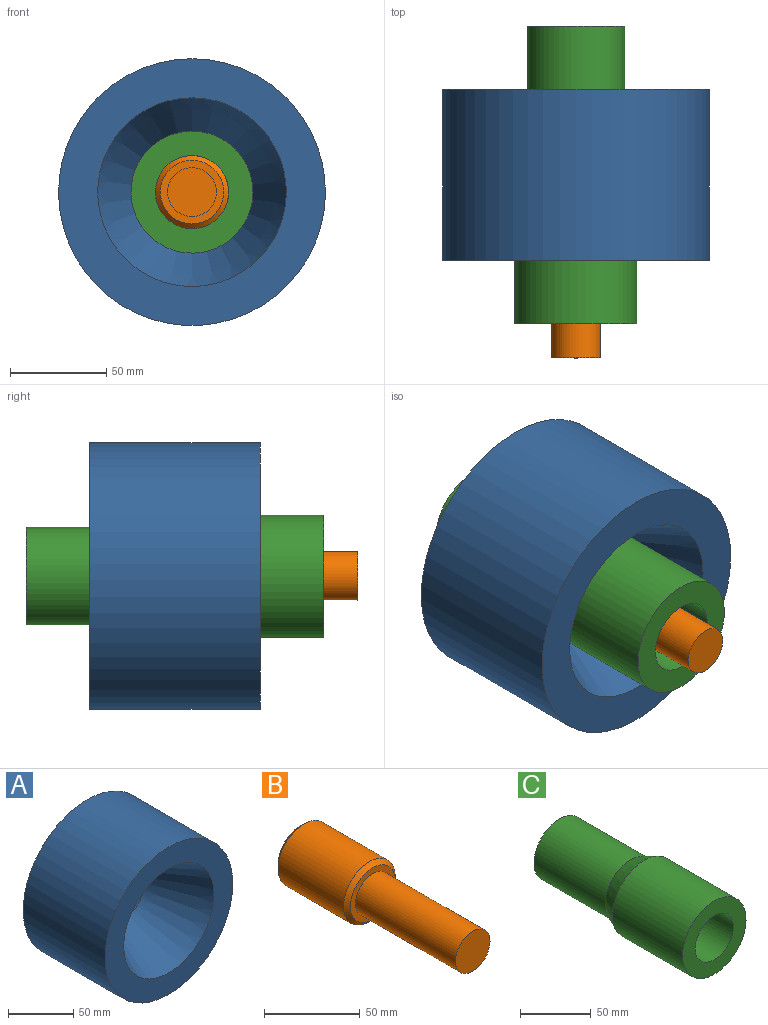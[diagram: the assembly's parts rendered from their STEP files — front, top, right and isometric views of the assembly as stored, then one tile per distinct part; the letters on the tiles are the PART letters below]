
ASSEMBLY  parts=3 mates=4
PART A: 6 faces, bbox 138.8x88.9x138.8 mm
  f0: cylinder r=69.42mm len=138.84mm, axis (0,1,0), area 38777.5mm2, adj f1,f5
  f1: plane 138.84x138.84mm, normal (0,-1,0), area 7570.5mm2, adj f0,f2
  f2: cone r=25.4mm half-angle=25deg, axis (0,-1,0), area 13116.8mm2, adj f1,f3
  f3: cylinder r=25.4mm len=50.8mm, axis (0,1,0), area 4053.7mm2, adj f2,f4
  f4: cone r=25.4mm half-angle=25deg, axis (0,1,0), area 2497.1mm2, adj f3,f5
  f5: plane 138.84x138.84mm, normal (0,1,0), area 12058.5mm2, adj f0,f4
PART B: 7 faces, bbox 38.1x127x38.1 mm
  f0: plane 33.02x33.02mm, normal (0,1,0), area 856.3mm2, adj f6
  f1: cylinder r=19.05mm len=48.26mm, axis (0,1,0), area 5776.5mm2, adj f5,f6
  f2: plane 33.02x33.02mm, normal (0,-1,0), area 349.6mm2, adj f3,f5
  f3: cylinder r=12.7mm len=73.66mm, axis (0,1,0), area 5877.8mm2, adj f2,f4
  f4: plane 25.4x25.4mm, normal (0,-1,0), area 506.7mm2, adj f3
  f5: cone r=19.05mm half-angle=45deg, axis (0,1,0), area 401.3mm2, adj f1,f2
  f6: cone r=16.51mm half-angle=45deg, axis (0,-1,0), area 401.3mm2, adj f0,f1
PART C: 6 faces, bbox 63.5x154.9x63.5 mm
  f0: plane 50.8x50.8mm, normal (0,1,0), area 886.7mm2, adj f1,f5
  f1: cylinder r=25.4mm len=71.12mm, axis (0,1,0), area 11350.2mm2, adj f0,f2
  f2: cone r=25.4mm half-angle=25deg, axis (0,-1,0), area 2697.7mm2, adj f1,f3
  f3: cylinder r=31.75mm len=70.2mm, axis (0,1,0), area 14004.8mm2, adj f2,f4
  f4: plane 63.5x63.5mm, normal (0,-1,0), area 2026.8mm2, adj f3,f5
  f5: cylinder r=19.05mm len=154.94mm, axis (0,1,0), area 18545.5mm2, adj f0,f4
PLACE A t=(0,12.7,0)mm
PLACE B rot(axis=(0,1,0),0deg) t=(0,12.7,0)mm
PLACE C rot(axis=(0,1,0),99.9deg) t=(0,12.7,0)mm
MATE cylindrical A.f0 <-> C.f1  axis (0,1,0) through (0,-12.7,0)mm
MATE cylindrical B.f1 <-> C.f1  axis (0,1,0) through (0,-2.54,0)mm
MATE planar B.f1 <-> A.f0  axis (0,1,0) through (0,0,0)mm
MATE planar A.f0 <-> C.f1  axis (0,1,0) through (0,12.7,0)mm
